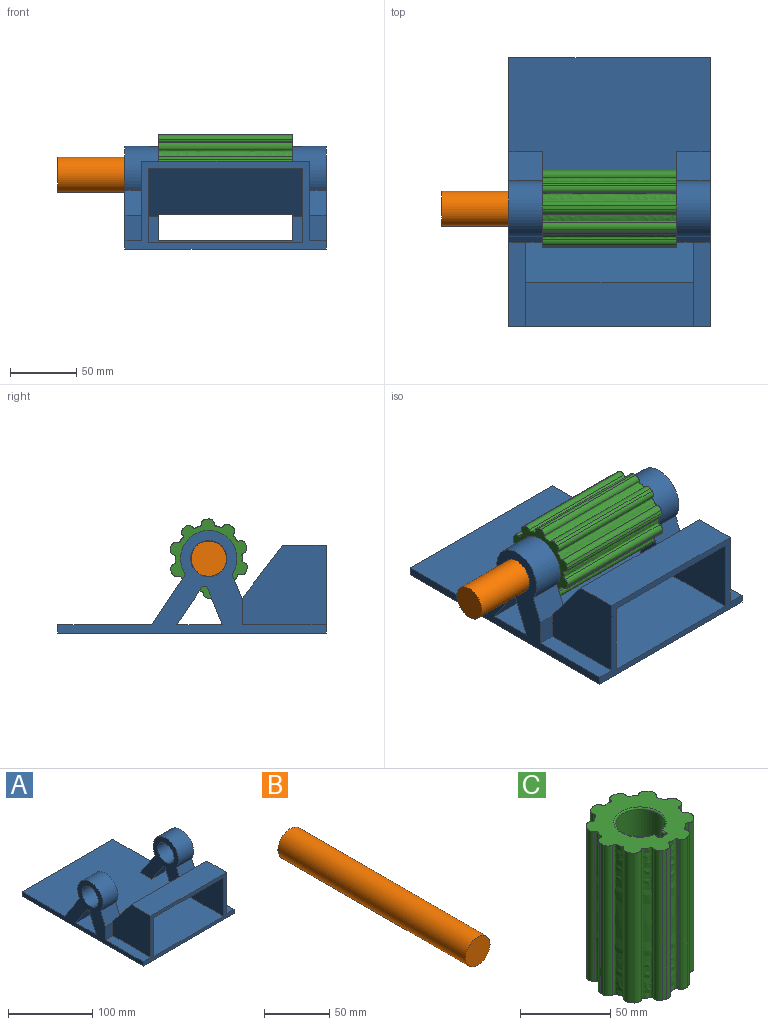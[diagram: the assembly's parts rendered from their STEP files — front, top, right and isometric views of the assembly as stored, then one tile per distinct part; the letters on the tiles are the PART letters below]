
ASSEMBLY  parts=3 mates=2
PART A: 39 faces, bbox 152.4x203.2x77.7 mm
  f0: plane 28.66x25.4mm, normal (0,-0.83,-0.56), area 875.8mm2, adj f4,f19,f22,f36
  f1: plane 38.1x25.47mm, normal (0,0.83,0.56), area 1164.1mm2, adj f5,f19,f22,f36
  f2: plane 25.4x19.05mm, normal (0,-0.93,0.37), area 521.8mm2, adj f5,f14,f19,f31,f36
  f3: plane 28.66x25.4mm, normal (0,0.93,-0.37), area 785.2mm2, adj f4,f19,f22,f36
  f4: plane 25.4x3.63mm, normal (0,0,-1), area 92.1mm2, adj f0,f3,f19,f36
  f5: cylinder r=21.34mm len=42.67mm, axis (-1,0,0), area 2343.8mm2, adj f1,f2,f19,f36
  f6: cylinder r=13.72mm len=27.43mm, axis (-1,0,0), area 2189mm2, adj f19,f36
  f7: plane 12.7x0.95mm, normal (0,1,0), area 12.1mm2, adj f12,f23,f26,f37
  f8: plane 117x19.66mm, normal (0,-1,0), area 440mm2, adj f9,f22,f27,f29,f30,f36,f37
  f9: plane 117x36.69mm, normal (0,-0.8,-0.61), area 5181.1mm2, adj f8,f28,f29,f30,f36,f37,f38
  f10: plane 28.66x25.4mm, normal (0,-0.83,-0.56), area 875.8mm2, adj f18,f22,f32,f37
  f11: plane 38.1x25.47mm, normal (0,0.83,0.56), area 1164.1mm2, adj f18,f22,f33,f37
  f12: plane 25.4x19.05mm, normal (0,-0.93,0.37), area 521.8mm2, adj f7,f18,f33,f34,f37
  f13: plane 28.66x25.4mm, normal (0,0.93,-0.37), area 785.2mm2, adj f18,f22,f32,f37
  f14: plane 12.7x0.95mm, normal (0,1,0), area 12.1mm2, adj f2,f23,f25,f36
  f15: plane 63.5x12.7mm, normal (0,0,1), area 806.4mm2, adj f17,f19,f25,f31
  f16: plane 63.5x12.7mm, normal (0,0,1), area 806.5mm2, adj f17,f18,f26,f34
  f17: plane 152.4x66.35mm, normal (0,-1,0), area 1994.8mm2, adj f15,f16,f18,f19,f21,f24,f25,f26
  f18: plane 203.2x77.69mm, normal (-1,0,0), area 3404.4mm2, adj f10,f11,f12,f13,f16,f17,f20,f21
  f19: plane 203.2x77.69mm, normal (1,0,0), area 3404.4mm2, adj f0,f1,f2,f3,f4,f5,f6,f15
  f20: plane 152.4x6.35mm, normal (0,1,0), area 967.7mm2, adj f18,f19,f21,f22
  f21: plane 203.2x152.4mm, normal (0,0,-1), area 30967.7mm2, adj f17,f18,f19,f20
  f22: plane 152.4x144.7mm, normal (0,0,1), area 20060mm2, adj f0,f1,f3,f8,f10,f11,f13,f18
  f23: plane 127x40mm, normal (0,0.8,0.61), area 6386.8mm2, adj f7,f14,f24,f25,f26,f38
  f24: plane 127x33.02mm, normal (0,0,1), area 4193.5mm2, adj f17,f23,f25,f26
  f25: plane 63.5x60mm, normal (1,0,0), area 3200.4mm2, adj f14,f15,f17,f23,f24,f31
  f26: plane 63.5x60mm, normal (-1,0,0), area 3200.4mm2, adj f7,f16,f17,f23,f24,f34
  f27: plane 117x58.5mm, normal (0,0,1), area 6844.5mm2, adj f8,f17,f29,f30
  f28: plane 117x30.54mm, normal (0,0,-1), area 3573.6mm2, adj f9,f17,f29,f30
  f29: plane 58.5x56.35mm, normal (-1,0,0), area 2783.6mm2, adj f8,f9,f17,f27,f28
  f30: plane 58.5x56.35mm, normal (1,0,0), area 2783.6mm2, adj f8,f9,f17,f27,f28
  f31: plane 19.05x12.7mm, normal (0,-1,0), area 241.9mm2, adj f2,f15,f19,f25
  f32: plane 25.4x3.63mm, normal (0,0,-1), area 92.1mm2, adj f10,f13,f18,f37
  f33: cylinder r=21.34mm len=42.67mm, axis (-1,0,0), area 2343.8mm2, adj f11,f12,f18,f37
  f34: plane 19.05x12.7mm, normal (0,-1,0), area 241.9mm2, adj f12,f16,f18,f26
  f35: cylinder r=13.72mm len=27.43mm, axis (-1,0,0), area 2189mm2, adj f18,f37
  f36: plane 74.87x71.34mm, normal (-1,0,0), area 2215.2mm2, adj f0,f1,f2,f3,f4,f5,f6,f8
  f37: plane 74.87x71.34mm, normal (1,0,0), area 2215.2mm2, adj f7,f8,f9,f10,f11,f12,f13,f22
  f38: plane 101.6x6.29mm, normal (0,0,-1), area 638.7mm2, adj f9,f23,f36,f37
PART B: 3 faces, bbox 26.7x203.2x26.7 mm
  f0: cylinder r=13.33mm len=203.2mm, axis (0,1,0), area 17025.4mm2, adj f1,f2
  f1: plane 26.67x26.67mm, normal (0,-1,0), area 558.6mm2, adj f0
  f2: plane 26.67x26.67mm, normal (0,1,0), area 558.6mm2, adj f0
PART C: 66 faces, bbox 60x58.1x101.6 mm
  f0: cylinder r=30mm len=101.6mm, axis (0,0,-1), area 249.8mm2, adj f10,f11,f37,f41
  f1: cylinder r=30mm len=101.6mm, axis (0,0,-1), area 249.8mm2, adj f10,f11,f34,f38
  f2: cylinder r=30mm len=101.6mm, axis (0,0,-1), area 249.8mm2, adj f10,f11,f31,f35
  f3: cylinder r=30mm len=101.6mm, axis (0,0,-1), area 249.8mm2, adj f10,f11,f28,f32
  f4: cylinder r=30mm len=101.6mm, axis (0,0,-1), area 249.8mm2, adj f10,f11,f25,f29
  f5: cylinder r=30mm len=101.6mm, axis (0,0,-1), area 249.8mm2, adj f10,f11,f22,f26
  f6: cylinder r=30mm len=101.6mm, axis (0,0,-1), area 249.8mm2, adj f10,f11,f19,f23
  f7: cylinder r=30mm len=101.6mm, axis (0,0,-1), area 249.8mm2, adj f10,f11,f16,f20
  f8: cylinder r=30mm len=101.6mm, axis (0,0,-1), area 249.8mm2, adj f10,f11,f13,f17
  f9: cylinder r=30mm len=101.6mm, axis (0,0,-1), area 249.8mm2, adj f10,f11,f14,f40
  f10: plane 60x58.06mm, normal (0,0,1), area 1732.1mm2, adj f0,f1,f2,f3,f4,f5,f6,f7
  f11: plane 60x58.06mm, normal (0,0,-1), area 1732.1mm2, adj f0,f1,f2,f3,f4,f5,f6,f7
  f12: extruded ~101.6x6.93mm, area 849.2mm2, adj f10,f11,f13,f14
  f13: cylinder r=3.81mm len=101.6mm, axis (0,0,1), area 584.6mm2, adj f8,f10,f11,f12
  f14: cylinder r=3.81mm len=101.6mm, axis (0,0,1), area 584.6mm2, adj f9,f10,f11,f12
  f15: extruded ~101.6x5.75mm, area 849.2mm2, adj f10,f11,f16,f17
  f16: cylinder r=3.81mm len=101.6mm, axis (0,0,1), area 584.6mm2, adj f7,f10,f11,f15
  f17: cylinder r=3.81mm len=101.6mm, axis (0,0,1), area 584.6mm2, adj f8,f10,f11,f15
  f18: extruded ~101.6x6.59mm, area 849.2mm2, adj f10,f11,f19,f20
  f19: cylinder r=3.81mm len=101.6mm, axis (0,0,1), area 584.6mm2, adj f6,f10,f11,f18
  f20: cylinder r=3.81mm len=101.6mm, axis (0,0,1), area 584.6mm2, adj f7,f10,f11,f18
  f21: extruded ~101.6x6.59mm, area 849.2mm2, adj f10,f11,f22,f23
  f22: cylinder r=3.81mm len=101.6mm, axis (0,0,1), area 584.6mm2, adj f5,f10,f11,f21
  f23: cylinder r=3.81mm len=101.6mm, axis (0,0,1), area 584.6mm2, adj f6,f10,f11,f21
  f24: extruded ~101.6x5.75mm, area 849.2mm2, adj f10,f11,f25,f26
  f25: cylinder r=3.81mm len=101.6mm, axis (0,0,1), area 584.6mm2, adj f4,f10,f11,f24
  f26: cylinder r=3.81mm len=101.6mm, axis (0,0,1), area 584.6mm2, adj f5,f10,f11,f24
  f27: extruded ~101.6x6.93mm, area 849.2mm2, adj f10,f11,f28,f29
  f28: cylinder r=3.81mm len=101.6mm, axis (0,0,1), area 584.6mm2, adj f3,f10,f11,f27
  f29: cylinder r=3.81mm len=101.6mm, axis (0,0,1), area 584.6mm2, adj f4,f10,f11,f27
  f30: extruded ~101.6x5.75mm, area 849.2mm2, adj f10,f11,f31,f32
  f31: cylinder r=3.81mm len=101.6mm, axis (0,0,1), area 584.6mm2, adj f2,f10,f11,f30
  f32: cylinder r=3.81mm len=101.6mm, axis (0,0,1), area 584.6mm2, adj f3,f10,f11,f30
  f33: extruded ~101.6x6.59mm, area 849.2mm2, adj f10,f11,f34,f35
  f34: cylinder r=3.81mm len=101.6mm, axis (0,0,1), area 584.6mm2, adj f1,f10,f11,f33
  f35: cylinder r=3.81mm len=101.6mm, axis (0,0,1), area 584.6mm2, adj f2,f10,f11,f33
  f36: extruded ~101.6x6.59mm, area 849.2mm2, adj f10,f11,f37,f38
  f37: cylinder r=3.81mm len=101.6mm, axis (0,0,1), area 584.6mm2, adj f0,f10,f11,f36
  f38: cylinder r=3.81mm len=101.6mm, axis (0,0,1), area 584.6mm2, adj f1,f10,f11,f36
  f39: extruded ~101.6x5.75mm, area 849.2mm2, adj f10,f11,f40,f41
  f40: cylinder r=3.81mm len=101.6mm, axis (0,0,1), area 584.6mm2, adj f9,f10,f11,f39
  f41: cylinder r=3.81mm len=101.6mm, axis (0,0,1), area 584.6mm2, adj f0,f10,f11,f39
  f42: plane 99.57x3.18mm, normal (-1,0,0), area 316.9mm2, adj f46,f49,f53,f62
  f43: plane 99.57x3.05mm, normal (0,1,0), area 303.5mm2, adj f46,f47,f57,f65
  f44: plane 99.57x3.18mm, normal (1,0,0), area 316.9mm2, adj f47,f48,f54,f61
  f45: cylinder r=13.53mm len=99.57mm, axis (0,0,-1), area 7882.6mm2, adj f48,f49,f50,f58
  f46: cylinder r=0.76mm len=99.57mm, axis (0,0,1), area 119.2mm2, adj f42,f43,f55,f64
  f47: cylinder r=0.76mm len=99.57mm, axis (0,0,-1), area 119.2mm2, adj f43,f44,f56,f63
  f48: cylinder r=0.76mm len=99.57mm, axis (0,0,-1), area 102.9mm2, adj f44,f45,f52,f59
  f49: cylinder r=0.76mm len=99.57mm, axis (0,0,-1), area 102.9mm2, adj f42,f45,f51,f60
  f50: torus R=14.54mm, axis (0,0,1), area 129.6mm2, adj f11,f45,f51,f52
  f51: bspline ~1.3x1.02mm, area 1.1mm2, adj f49,f50,f53
  f52: bspline ~1.3x1.02mm, area 1.1mm2, adj f48,f50,f54
  f53: cylinder r=1.02mm len=3.18mm, axis (0,-1,0), area 5mm2, adj f11,f42,f51,f55
  f54: cylinder r=1.02mm len=3.18mm, axis (0,1,0), area 5mm2, adj f11,f44,f52,f56
  f55: torus R=1.78mm, axis (0,0,1), area 2.8mm2, adj f11,f46,f53,f57
  f56: torus R=1.78mm, axis (0,0,1), area 2.8mm2, adj f11,f47,f54,f57
  f57: cylinder r=1.02mm len=3.05mm, axis (-1,0,0), area 4.9mm2, adj f11,f43,f55,f56
  f58: torus R=14.54mm, axis (0,0,1), area 129.6mm2, adj f10,f45,f59,f60
  f59: bspline ~1.3x1.02mm, area 1.1mm2, adj f48,f58,f61
  f60: bspline ~1.02x1.02mm, area 1.1mm2, adj f49,f58,f62
  f61: cylinder r=1.02mm len=3.18mm, axis (0,1,0), area 5mm2, adj f10,f44,f59,f63
  f62: cylinder r=1.02mm len=3.18mm, axis (0,-1,0), area 5mm2, adj f10,f42,f60,f64
  f63: torus R=1.78mm, axis (0,0,1), area 2.8mm2, adj f10,f47,f61,f65
  f64: torus R=1.78mm, axis (0,0,1), area 2.8mm2, adj f10,f46,f62,f65
  f65: cylinder r=1.02mm len=3.05mm, axis (-1,0,0), area 4.9mm2, adj f10,f43,f63,f64
PLACE A at identity fixed
PLACE B rot(axis=(0.63,-0.63,0.47),130deg) t=(-127,-12.7,50)mm
PLACE C rot(axis=(0.63,-0.47,-0.63),130deg) t=(50.8,-12.7,50)mm
MATE revolute B.f0 <-> C.f0  axis (1,0,0) through (76.2,-12.7,50)mm
MATE revolute B.f0 <-> A.f5  axis (1,0,0) through (76.2,-12.7,50)mm
